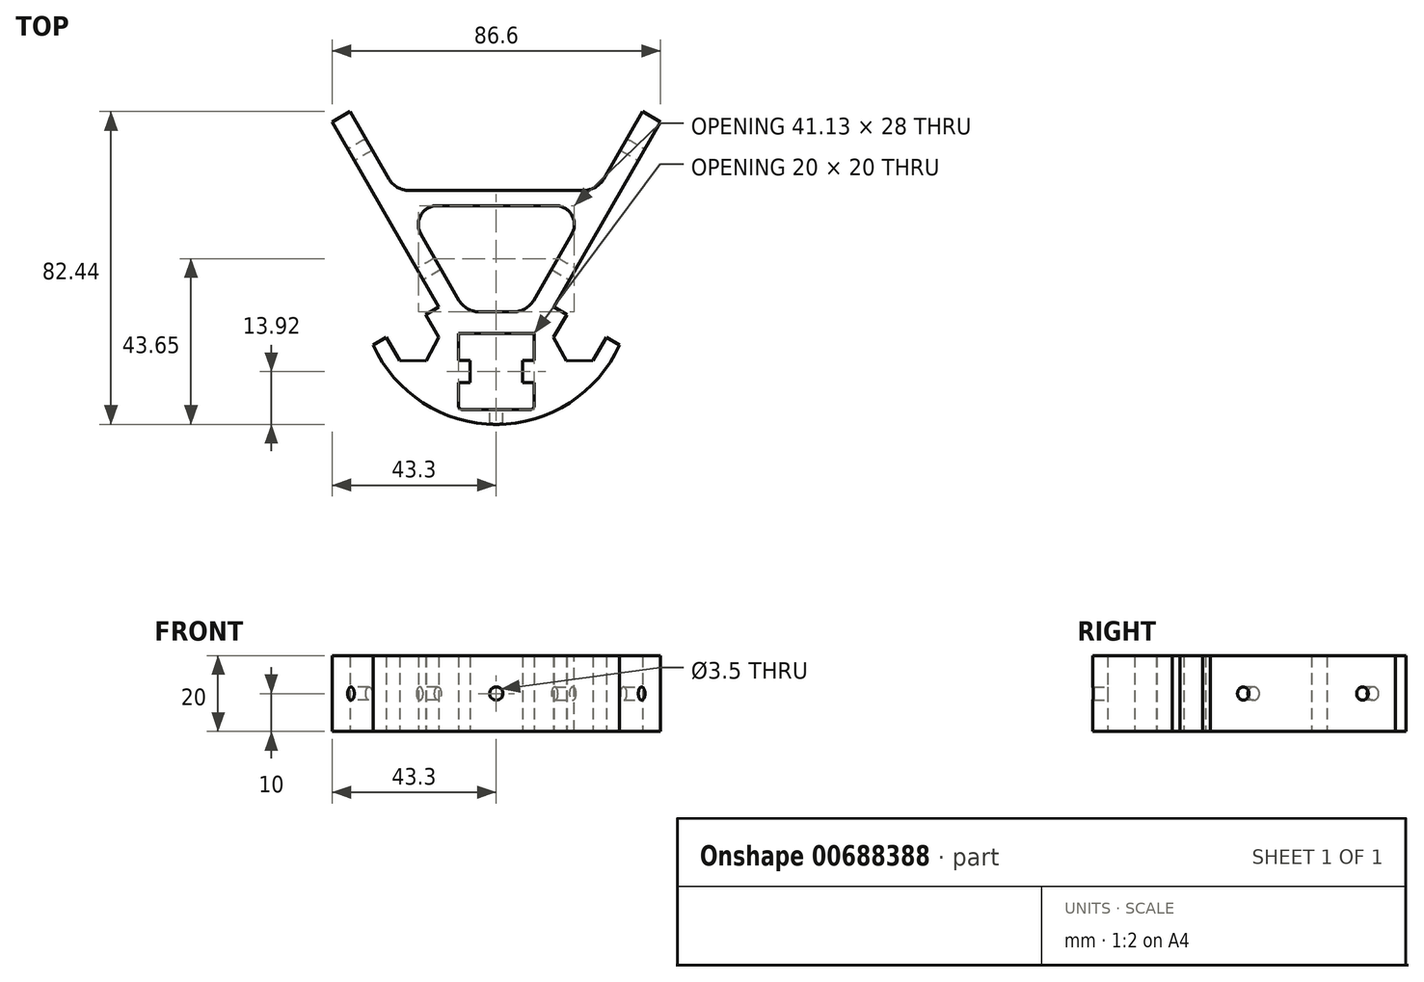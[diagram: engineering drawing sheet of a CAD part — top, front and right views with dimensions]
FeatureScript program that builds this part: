
annotation { "Feature Type Name" : "Feature", "Feature Type Description" : "" }
export const myFeature = defineFeature(function(context is Context, id is Id, definition is map)
    precondition{}
    {
        {
            var Q0;
            Q0=qCreatedBy(makeId("Top.planeOp"),FACE);
            var sketch = newSketch(context, id + "F0", { "sketchPlane" : qUnion([Q0])});
            skLineSegment(sketch, "E0", {"start": v(0, 0) * mm, "end": v(32.48, 0) * mm});
            skLineSegment(sketch, "E1", {"start": v(0, 0) * mm, "end": v(-32.48, 0) * mm});
            skArc(sketch, "E2", {"start": v(-32.48, 0) * mm, "mid": v(0, -20.94) * mm, "end": v(32.48, 0) * mm});
            skLineSegment(sketch, "E3", {"start": v(-32.48, 0) * mm, "end": v(-15.15, 10) * mm});
            skLineSegment(sketch, "E4", {"start": v(32.48, 0) * mm, "end": v(15.15, 10) * mm});
            skLineSegment(sketch, "E5", {"start": v(15.15, 10) * mm, "end": v(43.3, 58.75) * mm});
            skLineSegment(sketch, "E6", {"start": v(-15.15, 10) * mm, "end": v(-43.3, 58.75) * mm});
            skLineSegment(sketch, "E7", {"start": v(38.54, 61.5) * mm, "end": v(43.3, 58.75) * mm});
            skLineSegment(sketch, "E8.bottom", {"start": v(10, -17.02) * mm, "end": v(-10, -17.02) * mm});
            skLineSegment(sketch, "E8.top", {"start": v(10, 2.98) * mm, "end": v(-10, 2.98) * mm});
            skLineSegment(sketch, "E8.left", {"start": v(10, -17.02) * mm, "end": v(10, 2.98) * mm});
            skLineSegment(sketch, "E8.right", {"start": v(-10, -17.02) * mm, "end": v(-10, 2.98) * mm});
            skPoint(sketch, "E8.middle", {"position": v(0, -7.02) * mm});
            skLineSegment(sketch, "E9", {"start": v(-98.14, 8.7) * mm, "end": v(40.87, 8.7) * mm});
            skLineSegment(sketch, "E10", {"start": v(-43.3, 58.75) * mm, "end": v(-38.54, 61.5) * mm});
            skLineSegment(sketch, "E11", {"start": v(-38.54, 61.5) * mm, "end": v(-8.06, 8.7) * mm});
            skLineSegment(sketch, "E12", {"start": v(38.54, 61.5) * mm, "end": v(8.06, 8.7) * mm});
            skLineSegment(sketch, "E13", {"start": v(-98.14, 36.7) * mm, "end": v(34.35, 36.7) * mm});
            skLineSegment(sketch, "E14", {"start": v(-98.39, 40.7) * mm, "end": v(36.56, 40.7) * mm});
            skLineSegment(sketch, "E15.bottom", {"start": v(-10, -7.02) * mm, "end": v(-6.9, -7.02) * mm});
            skLineSegment(sketch, "E15.top", {"start": v(-10, -4.12) * mm, "end": v(-6.9, -4.12) * mm});
            skLineSegment(sketch, "E15.left", {"start": v(-10, -7.02) * mm, "end": v(-10, -4.12) * mm});
            skLineSegment(sketch, "E15.right", {"start": v(-6.9, -7.02) * mm, "end": v(-6.9, -4.12) * mm});
            skLineSegment(sketch, "E16.top", {"start": v(-10, -9.92) * mm, "end": v(-6.9, -9.92) * mm});
            skLineSegment(sketch, "E16.left", {"start": v(-10, -7.02) * mm, "end": v(-10, -9.92) * mm});
            skLineSegment(sketch, "E16.right", {"start": v(-6.9, -7.02) * mm, "end": v(-6.9, -9.92) * mm});
            skLineSegment(sketch, "E17.1.0", {"start": v(10, 2.98) * mm, "end": v(10, -17.02) * mm});
            skLineSegment(sketch, "E17.1.1", {"start": v(2.9, -17.02) * mm, "end": v(2.9, -13.92) * mm});
            skLineSegment(sketch, "E17.1.2", {"start": v(0, -17.02) * mm, "end": v(0, -13.92) * mm});
            skLineSegment(sketch, "E17.1.3", {"start": v(-2.9, -17.02) * mm, "end": v(-2.9, -13.92) * mm});
            skLineSegment(sketch, "E17.1.4", {"start": v(0, -13.92) * mm, "end": v(-2.9, -13.92) * mm});
            skLineSegment(sketch, "E17.1.5", {"start": v(0, -13.92) * mm, "end": v(2.9, -13.92) * mm});
            skLineSegment(sketch, "E17.2.0", {"start": v(-10, 2.98) * mm, "end": v(10, 2.98) * mm});
            skLineSegment(sketch, "E17.2.1", {"start": v(10, -4.12) * mm, "end": v(6.9, -4.12) * mm});
            skLineSegment(sketch, "E17.2.2", {"start": v(10, -7.02) * mm, "end": v(6.9, -7.02) * mm});
            skLineSegment(sketch, "E17.2.3", {"start": v(10, -9.92) * mm, "end": v(6.9, -9.92) * mm});
            skLineSegment(sketch, "E17.2.4", {"start": v(6.9, -7.02) * mm, "end": v(6.9, -9.92) * mm});
            skLineSegment(sketch, "E17.2.5", {"start": v(6.9, -7.02) * mm, "end": v(6.9, -4.12) * mm});
            skLineSegment(sketch, "E17.3.1", {"start": v(-2.9, 2.98) * mm, "end": v(-2.9, -0.12) * mm});
            skLineSegment(sketch, "E17.3.2", {"start": v(0, 2.98) * mm, "end": v(0, -0.12) * mm});
            skLineSegment(sketch, "E17.3.3", {"start": v(2.9, 2.98) * mm, "end": v(2.9, -0.12) * mm});
            skLineSegment(sketch, "E17.3.4", {"start": v(0, -0.12) * mm, "end": v(2.9, -0.12) * mm});
            skLineSegment(sketch, "E17.3.5", {"start": v(0, -0.12) * mm, "end": v(-2.9, -0.12) * mm});
            skLineSegment(sketch, "E18", {"start": v(18.62, 8) * mm, "end": v(15.12, 1.94) * mm});
            skLineSegment(sketch, "E19", {"start": v(29.01, 2) * mm, "end": v(25.51, -4.06) * mm});
            skPoint(sketch, "E20", {"position": v(23.81, 5) * mm});
            skLineSegment(sketch, "E21", {"start": v(15.12, 1.94) * mm, "end": v(18.51, -4.18) * mm});
            skLineSegment(sketch, "E22", {"start": v(25.51, -4.06) * mm, "end": v(18.51, -4.18) * mm});
            skLineSegment(sketch, "E23.MirrorCS", {"start": v(-18.62, 8) * mm, "end": v(-15.12, 1.94) * mm});
            skLineSegment(sketch, "E24.MirrorCS", {"start": v(-15.12, 1.94) * mm, "end": v(-18.51, -4.18) * mm});
            skLineSegment(sketch, "E25.MirrorCS", {"start": v(-25.51, -4.06) * mm, "end": v(-18.51, -4.18) * mm});
            skLineSegment(sketch, "E26.MirrorCS", {"start": v(-29.01, 2) * mm, "end": v(-25.51, -4.06) * mm});
            skSolve(sketch);
        }
        {
            var Q0;
            {var subQ5=sQuery(id+"F0.wireOp",EDGE,"E6");var subQ6=sQuery(id+"F0.wireOp",EDGE,"E3");var subQ7=makeQuery(id+"F0.imprint","INTERSECT",VERTEX,{"derivedFrom":[subQ6,subQ5]});Q0=makeQuery(id+"F0.imprint","IMPRINT",FACE,{"disambiguationData":[TD([[makeQuery(id+"F0.imprint","IMPRINT",EDGE,{"disambiguationData":[TD([[subQ7,1.0]])],"derivedFrom":subQ6}),-1.0]])]});}
            var Q1;
            {var subQ3=sQuery(id+"F0.wireOp",EDGE,"E4");var subQ7=sQuery(id+"F0.wireOp",EDGE,"E5");var subQ8=makeQuery(id+"F0.imprint","INTERSECT",VERTEX,{"derivedFrom":[subQ3,subQ7]});Q1=makeQuery(id+"F0.imprint","IMPRINT",FACE,{"disambiguationData":[TD([[makeQuery(id+"F0.imprint","IMPRINT",EDGE,{"disambiguationData":[TD([[subQ8,1.0]])],"derivedFrom":subQ3}),1.0]])]});}
            var Q2;
            {var subQ0=sQuery(id+"F0.wireOp",EDGE,"E10");Q2=makeQuery(id+"F0.imprint","IMPRINT",FACE,{"disambiguationData":[TD([[makeQuery(id+"F0.imprint","IMPRINT",EDGE,{"derivedFrom":subQ0}),-1.0]])]});}
            var Q3;
            {var subQ0=sQuery(id+"F0.wireOp",EDGE,"E13");var subQ1=sQuery(id+"F0.wireOp",EDGE,"E6");var subQ2=makeQuery(id+"F0.imprint","INTERSECT",VERTEX,{"derivedFrom":[subQ1,subQ0]});Q3=makeQuery(id+"F0.imprint","IMPRINT",FACE,{"disambiguationData":[TD([[makeQuery(id+"F0.imprint","IMPRINT",EDGE,{"disambiguationData":[TD([[subQ2,-1.0]])],"derivedFrom":subQ1}),-1.0]])]});}
            var Q4;
            {var subQ0=sQuery(id+"F0.wireOp",EDGE,"E13");var subQ1=sQuery(id+"F0.wireOp",EDGE,"E5");var subQ2=makeQuery(id+"F0.imprint","INTERSECT",VERTEX,{"derivedFrom":[subQ1,subQ0]});Q4=makeQuery(id+"F0.imprint","IMPRINT",FACE,{"disambiguationData":[TD([[makeQuery(id+"F0.imprint","IMPRINT",EDGE,{"disambiguationData":[TD([[subQ2,-1.0]])],"derivedFrom":subQ1}),1.0]])]});}
            var Q5;
            {var subQ0=sQuery(id+"F0.wireOp",EDGE,"E7");Q5=makeQuery(id+"F0.imprint","IMPRINT",FACE,{"disambiguationData":[TD([[makeQuery(id+"F0.imprint","IMPRINT",EDGE,{"derivedFrom":subQ0}),-1.0]])]});}
            var Q6;
            {var subQ19=sQuery(id+"F0.wireOp",EDGE,"E2");Q6=makeQuery(id+"F0.imprint","IMPRINT",FACE,{"disambiguationData":[TD([[makeQuery(id+"F0.imprint","IMPRINT",EDGE,{"derivedFrom":subQ19}),1.0]])]});}
            var Q7;
            {var subQ20=sQuery(id+"F0.wireOp",EDGE,"E18");Q7=makeQuery(id+"F0.imprint","IMPRINT",FACE,{"disambiguationData":[TD([[makeQuery(id+"F0.imprint","IMPRINT",EDGE,{"derivedFrom":subQ20}),-1.0]])]});}
            var Q8;
            {var subQ0=sQuery(id+"F0.wireOp",EDGE,"E15.top");Q8=makeQuery(id+"F0.imprint","IMPRINT",FACE,{"disambiguationData":[TD([[makeQuery(id+"F0.imprint","IMPRINT",EDGE,{"derivedFrom":subQ0}),-1.0]])]});}
            var Q9;
            {var subQ0=sQuery(id+"F0.wireOp",EDGE,"E15.bottom");Q9=makeQuery(id+"F0.imprint","IMPRINT",FACE,{"disambiguationData":[TD([[makeQuery(id+"F0.imprint","IMPRINT",EDGE,{"derivedFrom":subQ0}),-1.0]])]});}
            var Q10;
            {var subQ0=sQuery(id+"F0.wireOp",EDGE,"E17.2.2");Q10=makeQuery(id+"F0.imprint","IMPRINT",FACE,{"disambiguationData":[TD([[makeQuery(id+"F0.imprint","IMPRINT",EDGE,{"derivedFrom":subQ0}),1.0]])]});}
            var Q11;
            {var subQ0=sQuery(id+"F0.wireOp",EDGE,"E17.2.1");Q11=makeQuery(id+"F0.imprint","IMPRINT",FACE,{"disambiguationData":[TD([[makeQuery(id+"F0.imprint","IMPRINT",EDGE,{"derivedFrom":subQ0}),1.0]])]});}
            var Q12;
            {var subQ0=sQuery(id+"F0.wireOp",EDGE,"E17.3.2");var subQ5=sQuery(id+"F0.wireOp",EDGE,"E17.2.0");var subQ6=makeQuery(id+"F0.imprint","INTERSECT",VERTEX,{"derivedFrom":[subQ5,subQ0]});Q12=makeQuery(id+"F0.imprint","IMPRINT",FACE,{"disambiguationData":[TD([[makeQuery(id+"F0.imprint","IMPRINT",EDGE,{"disambiguationData":[TD([[subQ6,-1.0]])],"derivedFrom":subQ5}),-1.0]])]});}
            var Q13;
            {var subQ3=sQuery(id+"F0.wireOp",EDGE,"E17.3.1");var subQ5=sQuery(id+"F0.wireOp",EDGE,"E17.2.0");var subQ6=makeQuery(id+"F0.imprint","INTERSECT",VERTEX,{"derivedFrom":[subQ5,subQ3]});Q13=makeQuery(id+"F0.imprint","IMPRINT",FACE,{"disambiguationData":[TD([[makeQuery(id+"F0.imprint","IMPRINT",EDGE,{"disambiguationData":[TD([[subQ6,-1.0]])],"derivedFrom":subQ5}),-1.0]])]});}
            var Q14;
            {var subQ0=sQuery(id+"F0.wireOp",EDGE,"E3");var subQ3=sQuery(id+"F0.wireOp",EDGE,"E26.MirrorCS");var subQ5=makeQuery(id+"F0.imprint","INTERSECT",VERTEX,{"derivedFrom":[subQ0,subQ3]});Q14=makeQuery(id+"F0.imprint","IMPRINT",FACE,{"disambiguationData":[TD([[makeQuery(id+"F0.imprint","IMPRINT",EDGE,{"disambiguationData":[TD([[subQ5,-1.0]])],"derivedFrom":subQ3}),-1.0]])]});}
            var Q15;
            {var subQ0=sQuery(id+"F0.wireOp",EDGE,"E4");var subQ3=sQuery(id+"F0.wireOp",EDGE,"E19");var subQ5=makeQuery(id+"F0.imprint","INTERSECT",VERTEX,{"derivedFrom":[subQ0,subQ3]});Q15=makeQuery(id+"F0.imprint","IMPRINT",FACE,{"disambiguationData":[TD([[makeQuery(id+"F0.imprint","IMPRINT",EDGE,{"disambiguationData":[TD([[subQ5,-1.0]])],"derivedFrom":subQ3}),1.0]])]});}
            var Q16;
            {var subQ0=sQuery(id+"F0.wireOp",EDGE,"E14");var subQ1=sQuery(id+"F0.wireOp",EDGE,"E11");var subQ2=makeQuery(id+"F0.imprint","INTERSECT",VERTEX,{"derivedFrom":[subQ1,subQ0]});Q16=makeQuery(id+"F0.imprint","IMPRINT",FACE,{"disambiguationData":[TD([[makeQuery(id+"F0.imprint","IMPRINT",EDGE,{"disambiguationData":[TD([[subQ2,-1.0]])],"derivedFrom":subQ1}),1.0]])]});}
            extrude(context, id + "F1", {"entities" : qUnion([Q0, Q1, Q2, Q3, Q4, Q5, Q6, Q7, Q8, Q9, Q10, Q11, Q12, Q13, Q14, Q15, Q16]), "depth" : 20 * mm});
        }
        {
            var Q0;
            Q0=makeQuery(id+"F1.opExtrude","SWEPT_EDGE",EDGE,{"disambiguationData":[OSD([sQuery(id+"F0.wireOp",EDGE,"E8.bottom"),sQuery(id+"F0.wireOp",EDGE,"E17.1.0")])]});
            var Q1;
            Q1=makeQuery(id+"F1.opExtrude","SWEPT_EDGE",EDGE,{"disambiguationData":[OSD([sQuery(id+"F0.wireOp",EDGE,"E8.bottom"),sQuery(id+"F0.wireOp",EDGE,"E8.right")])]});
            var Q2;
            Q2=makeQuery(id+"F1.opExtrude","SWEPT_EDGE",EDGE,{"disambiguationData":[OSD([sQuery(id+"F0.wireOp",EDGE,"E17.2.0"),sQuery(id+"F0.wireOp",EDGE,"E8.right")])]});
            var Q3;
            Q3=makeQuery(id+"F1.opExtrude","SWEPT_EDGE",EDGE,{"disambiguationData":[OSD([sQuery(id+"F0.wireOp",EDGE,"E17.1.0"),sQuery(id+"F0.wireOp",EDGE,"E17.2.0")])]});
            fillet(context, id + "F2", {"entities" : qUnion([Q0, Q1, Q2, Q3]), "radius" : 1 * mm, "tangentPropagation" : true, "allowEdgeOverflow" : false});
        }
        {
            var Q0;
            Q0=makeQuery(id+"F1.opExtrude","SWEPT_EDGE",EDGE,{"disambiguationData":[OSD([sQuery(id+"F0.wireOp",EDGE,"E9"),sQuery(id+"F0.wireOp",EDGE,"E11")])]});
            var Q1;
            Q1=makeQuery(id+"F1.opExtrude","SWEPT_EDGE",EDGE,{"disambiguationData":[OSD([sQuery(id+"F0.wireOp",EDGE,"E9"),sQuery(id+"F0.wireOp",EDGE,"E12")])]});
            var Q2;
            Q2=makeQuery(id+"F1.opExtrude","SWEPT_EDGE",EDGE,{"disambiguationData":[OSD([sQuery(id+"F0.wireOp",EDGE,"E12"),sQuery(id+"F0.wireOp",EDGE,"E14")])]});
            var Q3;
            Q3=makeQuery(id+"F1.opExtrude","SWEPT_EDGE",EDGE,{"disambiguationData":[OSD([sQuery(id+"F0.wireOp",EDGE,"E11"),sQuery(id+"F0.wireOp",EDGE,"E14")])]});
            fillet(context, id + "F3", {"entities" : qUnion([Q0, Q1, Q2, Q3]), "radius" : 6 * mm, "tangentPropagation" : true, "allowEdgeOverflow" : false});
        }
        {
            var Q0;
            Q0=makeQuery(id+"F1.opExtrude","SWEPT_FACE",FACE,{"disambiguationData":[OSD([sQuery(id+"F0.wireOp",EDGE,"E5")])]});
            var sketch = newSketch(context, id + "F4", { "sketchPlane" : qUnion([Q0])});
            skCircle(sketch, "E27", {"center": v(26.24, 10) * mm, "radius": 1.75 * mm});
            skCircle(sketch, "E28", {"center": v(62.53, 10) * mm, "radius": 1.75 * mm});
            skSolve(sketch);
        }
        {
            var Q0;
            Q0=qSketchRegion(id+"F4",true);
            var Q1;
            {var subQ0=sQuery(id+"F0.wireOp",EDGE,"E12");Q1=makeQuery(id+"F1.opExtrude","SWEPT_FACE",FACE,{"disambiguationData":[OSD([subQ0]),TDD([makeQuery(id+"F0.imprint","IMPRINT",EDGE,{"disambiguationData":[TD([[makeQuery(id+"F0.imprint","INTERSECT",VERTEX,{"derivedFrom":[sQuery(id+"F0.wireOp",EDGE,"E9"),subQ0]}),1.0]])],"derivedFrom":subQ0})])]});}
            extrude(context, id + "F5", {"entities" : qUnion([Q0]), "operationType" : NewBodyOperationType.REMOVE, "endBound" : BoundingType.UP_TO_SURFACE, "oppositeDirection" : true, "endBoundEntityFace" : qUnion([Q1]), "depth" : 25 * mm});
        }
        {
            var Q0;
            Q0=makeQuery(id+"F1.opExtrude","SWEPT_FACE",FACE,{"disambiguationData":[OSD([sQuery(id+"F0.wireOp",EDGE,"E8.bottom")])]});
            var sketch = newSketch(context, id + "F6", { "sketchPlane" : qUnion([Q0])});
            skCircle(sketch, "E29", {"center": v(0, 10) * mm, "radius": 1.75 * mm});
            skSolve(sketch);
        }
        {
            var Q0;
            Q0=makeQuery(id+"F6.imprint","IMPRINT",FACE,{"disambiguationData":[TD([[makeQuery(id+"F6.imprint","IMPRINT",EDGE,{"derivedFrom":sQuery(id+"F6.wireOp",EDGE,"E29")}),1.0]])]});
            var Q1;
            Q1=makeQuery(id+"F1.opExtrude","SWEPT_FACE",FACE,{"disambiguationData":[OSD([sQuery(id+"F0.wireOp",EDGE,"E2")])]});
            extrude(context, id + "F7", {"entities" : qUnion([Q0]), "operationType" : NewBodyOperationType.REMOVE, "endBound" : BoundingType.UP_TO_SURFACE, "oppositeDirection" : true, "endBoundEntityFace" : qUnion([Q1]), "depth" : 25 * mm});
        }
        {
            var Q0;
            Q0=makeQuery(id+"F1.opExtrude","SWEPT_BODY",BODY,{"disambiguationData":[OSD([sQuery(id+"F0.wireOp",EDGE,"E0"),sQuery(id+"F0.wireOp",EDGE,"E1"),sQuery(id+"F0.wireOp",EDGE,"E2"),sQuery(id+"F0.wireOp",EDGE,"E3"),sQuery(id+"F0.wireOp",EDGE,"E4"),sQuery(id+"F0.wireOp",EDGE,"E5"),sQuery(id+"F0.wireOp",EDGE,"E6"),sQuery(id+"F0.wireOp",EDGE,"E7"),sQuery(id+"F0.wireOp",EDGE,"E8.bottom"),sQuery(id+"F0.wireOp",EDGE,"E9"),sQuery(id+"F0.wireOp",EDGE,"E10"),sQuery(id+"F0.wireOp",EDGE,"E11"),sQuery(id+"F0.wireOp",EDGE,"E12"),sQuery(id+"F0.wireOp",EDGE,"E13"),sQuery(id+"F0.wireOp",EDGE,"E14"),sQuery(id+"F0.wireOp",EDGE,"E15.top"),sQuery(id+"F0.wireOp",EDGE,"E15.right"),sQuery(id+"F0.wireOp",EDGE,"E16.top"),sQuery(id+"F0.wireOp",EDGE,"E16.right"),sQuery(id+"F0.wireOp",EDGE,"E17.1.0"),sQuery(id+"F0.wireOp",EDGE,"E17.2.0"),sQuery(id+"F0.wireOp",EDGE,"E17.2.1"),sQuery(id+"F0.wireOp",EDGE,"E17.2.3"),sQuery(id+"F0.wireOp",EDGE,"E17.2.4"),sQuery(id+"F0.wireOp",EDGE,"E17.2.5"),sQuery(id+"F0.wireOp",EDGE,"E8.right"),sQuery(id+"F0.wireOp",EDGE,"E17.3.1"),sQuery(id+"F0.wireOp",EDGE,"E17.3.3"),sQuery(id+"F0.wireOp",EDGE,"E18"),sQuery(id+"F0.wireOp",EDGE,"E19"),sQuery(id+"F0.wireOp",EDGE,"E21"),sQuery(id+"F0.wireOp",EDGE,"E22"),sQuery(id+"F0.wireOp",EDGE,"E23.MirrorCS"),sQuery(id+"F0.wireOp",EDGE,"E24.MirrorCS"),sQuery(id+"F0.wireOp",EDGE,"E25.MirrorCS"),sQuery(id+"F0.wireOp",EDGE,"E26.MirrorCS")])]});
            transform(context, id + "F8", {"entities" : qUnion([Q0]), "transformType" : TransformType.TRANSLATION_3D, "dx" : 0 * mm, "dy" : 7.02 * mm, "dz" : 0 * mm, "makeCopy" : false});
        }
        {
            var Q0;
            Q0=makeQuery(id+"F1.opExtrude","SWEPT_BODY",BODY,{"disambiguationData":[OSD([sQuery(id+"F0.wireOp",EDGE,"E0"),sQuery(id+"F0.wireOp",EDGE,"E1"),sQuery(id+"F0.wireOp",EDGE,"E2"),sQuery(id+"F0.wireOp",EDGE,"E3"),sQuery(id+"F0.wireOp",EDGE,"E4"),sQuery(id+"F0.wireOp",EDGE,"E5"),sQuery(id+"F0.wireOp",EDGE,"E6"),sQuery(id+"F0.wireOp",EDGE,"E7"),sQuery(id+"F0.wireOp",EDGE,"E8.bottom"),sQuery(id+"F0.wireOp",EDGE,"E9"),sQuery(id+"F0.wireOp",EDGE,"E10"),sQuery(id+"F0.wireOp",EDGE,"E11"),sQuery(id+"F0.wireOp",EDGE,"E12"),sQuery(id+"F0.wireOp",EDGE,"E13"),sQuery(id+"F0.wireOp",EDGE,"E14"),sQuery(id+"F0.wireOp",EDGE,"E15.top"),sQuery(id+"F0.wireOp",EDGE,"E15.right"),sQuery(id+"F0.wireOp",EDGE,"E16.top"),sQuery(id+"F0.wireOp",EDGE,"E16.right"),sQuery(id+"F0.wireOp",EDGE,"E17.1.0"),sQuery(id+"F0.wireOp",EDGE,"E17.2.0"),sQuery(id+"F0.wireOp",EDGE,"E17.2.1"),sQuery(id+"F0.wireOp",EDGE,"E17.2.3"),sQuery(id+"F0.wireOp",EDGE,"E17.2.4"),sQuery(id+"F0.wireOp",EDGE,"E17.2.5"),sQuery(id+"F0.wireOp",EDGE,"E8.right"),sQuery(id+"F0.wireOp",EDGE,"E17.3.1"),sQuery(id+"F0.wireOp",EDGE,"E17.3.3"),sQuery(id+"F0.wireOp",EDGE,"E18"),sQuery(id+"F0.wireOp",EDGE,"E19"),sQuery(id+"F0.wireOp",EDGE,"E21"),sQuery(id+"F0.wireOp",EDGE,"E22"),sQuery(id+"F0.wireOp",EDGE,"E23.MirrorCS"),sQuery(id+"F0.wireOp",EDGE,"E24.MirrorCS"),sQuery(id+"F0.wireOp",EDGE,"E25.MirrorCS"),sQuery(id+"F0.wireOp",EDGE,"E26.MirrorCS")])]});
            var Q1;
            Q1=qCreatedBy(makeId("Right.planeOp"),FACE);
            mirror(context, id + "F9", {"operationType" : NewBodyOperationType.INTERSECT, "entities" : qUnion([Q0]), "mirrorPlane" : qUnion([Q1])});
        }
        {
            var Q0;
            Q0=makeQuery(id+"F1.opExtrude","SWEPT_EDGE",EDGE,{"disambiguationData":[OSD([sQuery(id+"F0.wireOp",EDGE,"E12"),sQuery(id+"F0.wireOp",EDGE,"E13")])]});
            var Q1;
            Q1=makeQuery(id+"F1.opExtrude","SWEPT_EDGE",EDGE,{"disambiguationData":[OSD([sQuery(id+"F0.wireOp",EDGE,"E11"),sQuery(id+"F0.wireOp",EDGE,"E13")])]});
            fillet(context, id + "F10", {"entities" : qUnion([Q0, Q1]), "radius" : 5 * mm, "tangentPropagation" : true, "allowEdgeOverflow" : false});
        }
    });
